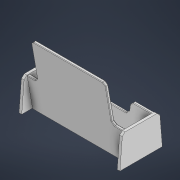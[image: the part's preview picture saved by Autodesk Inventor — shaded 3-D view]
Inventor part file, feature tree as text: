
AUTODESK INVENTOR PART (.ipt)
format: ipt  version: 2021 (Build 250183000, 183)  size: 3,301,376 bytes
history: native  units: mm
features: extrude x5, sketch x5, other x4, chamfer x2, mirror x1
ambient origin geometry x8: Origin, YZ Plane, XZ Plane, XY Plane, X Axis, Y Axis, Z Axis, Center Point
bodies: Solid1 (feature_tree)
feature tree (17):
  other  "Blocks"
  extrude  "Extrusion1"  Depth=35.0mm
  extrude  "Extrusion2"  TaperAngle=0.0deg  [1 undecoded]
  extrude  "Extrusion5"  Depth=2.5mm
  extrude  "Extrusion6"  Depth=2.5mm
  chamfer  "Chamfer1"  Distance=17.453293mm
  chamfer  "Chamfer2"  Distance=17.453293mm
  mirror  "Mirror2"
  extrude  "Extrusion7"  Depth=45.0mm TaperAngle=0.0deg
  sketch  "Sketch2"  dims[d4=30.0mm d5=35.0mm]
  sketch  "Sketch5"  dims[d6=40.0mm d14=0.0mm]
  sketch  "Sketch8"  dims[d15=2.5mm d16=2.5mm]
  sketch  "Sketch9"  dims[d17=2.5mm d18=2.5mm]
  sketch  "Sketch10"  dims[d19=2.5mm d22=17.453293mm d23=17.453293mm d24=45.0mm d25=0.0mm d33=10.0mm d34=25.0mm d35=2.5mm d36=0.0mm d38=10.0mm d39=2.5mm d40=0.0mm d43=65.0mm d44=2.5mm d45=2.0mm d46=45.0deg d47=0.5mm d48=2.0mm d49=45.0deg d50=1.5mm d51=0.0mm]
  other  "lgcc"
  other  "lgcc2"
  other  "lgcc2:1"
note: 1 required parameter value undecoded (feature->parameter linkage not recoverable at this tier; creation-order binding heuristic only, values carry confidence <= 0.55)
